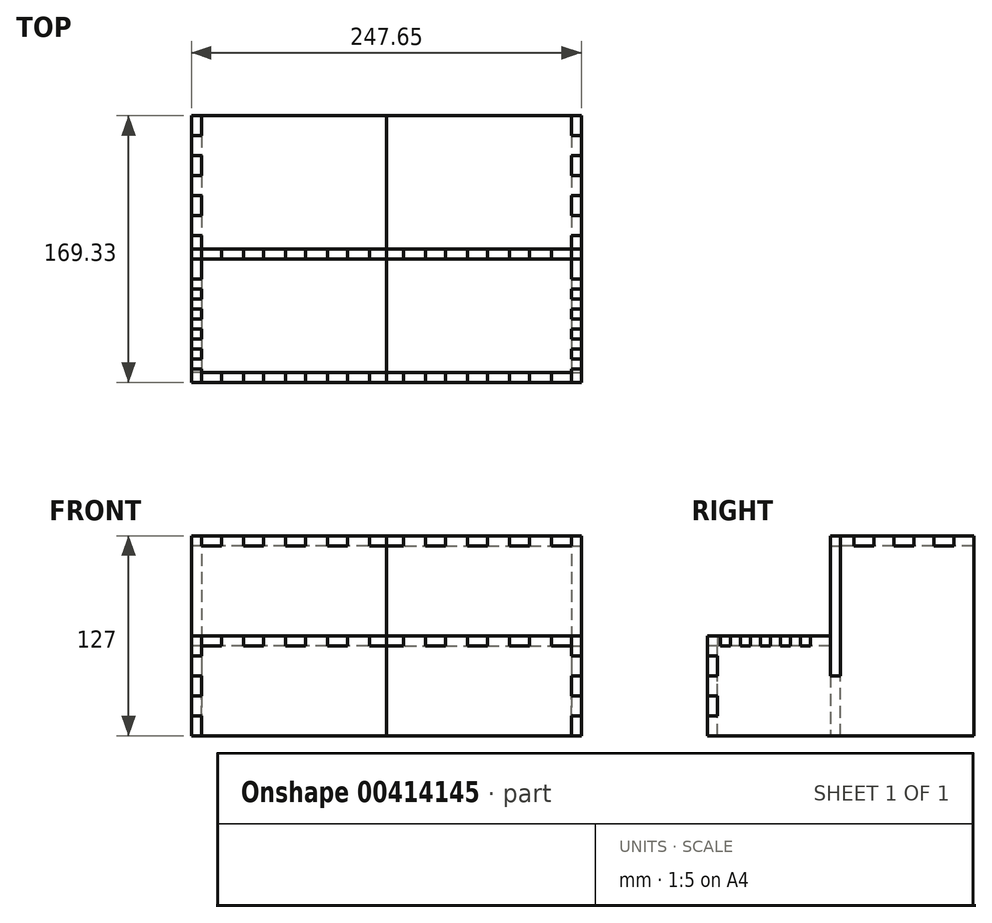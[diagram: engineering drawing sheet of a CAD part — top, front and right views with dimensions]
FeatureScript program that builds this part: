
annotation { "Feature Type Name" : "Feature", "Feature Type Description" : "" }
export const myFeature = defineFeature(function(context is Context, id is Id, definition is map)
    precondition{}
    {
        {
            var Q0;
            Q0=qCreatedBy(makeId("Front.planeOp"),FACE);
            cPlane(context, id + "F0", {"entities" : qUnion([Q0]), "cplaneType" : CPlaneType.OFFSET, "offset" : 84.67 * mm, "oppositeDirection" : true, "width" : 152.4 * mm, "height" : 152.4 * mm});
        }
        {
            var Q0;
            Q0=qCreatedBy(id+"F0.planeOp",FACE);
            cPlane(context, id + "F1", {"entities" : qUnion([Q0]), "cplaneType" : CPlaneType.OFFSET, "offset" : 84.67 * mm, "oppositeDirection" : true, "width" : 152.4 * mm, "height" : 152.4 * mm});
        }
        {
            var Q0;
            Q0=qCreatedBy(makeId("Top.planeOp"),FACE);
            cPlane(context, id + "F2", {"entities" : qUnion([Q0]), "cplaneType" : CPlaneType.OFFSET, "offset" : 127 * mm, "oppositeDirection" : true, "width" : 152.4 * mm, "height" : 152.4 * mm});
        }
        {
            var Q0;
            Q0=qCreatedBy(id+"F2.planeOp",FACE);
            cPlane(context, id + "F3", {"entities" : qUnion([Q0]), "cplaneType" : CPlaneType.OFFSET, "offset" : 63.5 * mm, "width" : 152.4 * mm, "height" : 152.4 * mm});
        }
        {
            var Q0;
            Q0=qCreatedBy(makeId("Right.planeOp"),FACE);
            cPlane(context, id + "F4", {"entities" : qUnion([Q0]), "cplaneType" : CPlaneType.OFFSET, "offset" : 247.65 * mm, "oppositeDirection" : true, "width" : 152.4 * mm, "height" : 152.4 * mm});
        }
        {
            var Q0;
            Q0=qCreatedBy(id+"F4.planeOp",FACE);
            cPlane(context, id + "F5", {"entities" : qUnion([Q0]), "cplaneType" : CPlaneType.OFFSET, "offset" : 123.82 * mm, "width" : 152.4 * mm, "height" : 152.4 * mm});
        }
        {
            var Q0;
            Q0=qCreatedBy(id+"F2.planeOp",FACE);
            var sketch = newSketch(context, id + "F6", { "sketchPlane" : qUnion([Q0])});
            skLineSegment(sketch, "E0", {"start": v(-247.65, 169.33) * mm, "end": v(-247.65, 0) * mm});
            skLineSegment(sketch, "E1", {"start": v(-241.3, 169.33) * mm, "end": v(-241.3, 0) * mm});
            skLineSegment(sketch, "E2", {"start": v(-247.65, 169.33) * mm, "end": v(-241.3, 169.33) * mm});
            skLineSegment(sketch, "E3", {"start": v(-247.65, 0) * mm, "end": v(-241.3, 0) * mm});
            skSolve(sketch);
        }
        {
            var Q0;
            Q0=makeQuery(id+"F6.imprint","IMPRINT",FACE,{"disambiguationData":[TD([[makeQuery(id+"F6.imprint","IMPRINT",EDGE,{"derivedFrom":sQuery(id+"F6.wireOp",EDGE,"E0")}),1.0]])]});
            var Q1;
            Q1=sQuery(id+"F6.wireOp",EDGE,"E0");
            var Q2;
            Q2=qCreatedBy(makeId("Top.planeOp"),FACE);
            extrude(context, id + "F7", {"entities" : qUnion([Q0]), "surfaceEntities" : qUnion([Q1]), "endBound" : BoundingType.UP_TO_SURFACE, "endBoundEntityFace" : qUnion([Q2]), "depth" : 25.4 * mm});
        }
        {
            var Q0;
            Q0=qCreatedBy(id+"F4.planeOp",FACE);
            var sketch = newSketch(context, id + "F8", { "sketchPlane" : qUnion([Q0])});
            skLineSegment(sketch, "E4", {"start": v(0, -63.5) * mm, "end": v(84.67, -63.5) * mm});
            skLineSegment(sketch, "E5", {"start": v(84.67, -63.5) * mm, "end": v(84.67, 0) * mm});
            skLineSegment(sketch, "E6", {"start": v(84.67, 0) * mm, "end": v(0, 0) * mm});
            skLineSegment(sketch, "E7", {"start": v(0, 0) * mm, "end": v(0, -63.5) * mm});
            skLineSegment(sketch, "E8", {"start": v(84.67, -63.5) * mm, "end": v(84.67, -88.9) * mm});
            skLineSegment(sketch, "E9", {"start": v(84.67, -88.9) * mm, "end": v(78.32, -88.9) * mm});
            skLineSegment(sketch, "E10", {"start": v(78.32, -88.9) * mm, "end": v(78.32, -63.5) * mm});
            skLineSegment(sketch, "E11", {"start": v(156.63, 0) * mm, "end": v(156.63, -6.35) * mm});
            skLineSegment(sketch, "E12", {"start": v(156.63, -6.35) * mm, "end": v(143.93, -6.35) * mm});
            skLineSegment(sketch, "E13", {"start": v(143.93, -6.35) * mm, "end": v(143.93, 0) * mm});
            skLineSegment(sketch, "E14", {"start": v(156.63, 0) * mm, "end": v(143.93, 0) * mm});
            skLineSegment(sketch, "E15.1.0.0", {"start": v(131.23, 0) * mm, "end": v(118.53, 0) * mm});
            skLineSegment(sketch, "E15.1.0.1", {"start": v(118.53, -6.35) * mm, "end": v(118.53, 0) * mm});
            skLineSegment(sketch, "E15.1.0.2", {"start": v(131.23, 0) * mm, "end": v(131.23, -6.35) * mm});
            skLineSegment(sketch, "E15.1.0.3", {"start": v(131.23, -6.35) * mm, "end": v(118.53, -6.35) * mm});
            skLineSegment(sketch, "E15.2.0.0", {"start": v(105.83, 0) * mm, "end": v(93.13, 0) * mm});
            skLineSegment(sketch, "E15.2.0.1", {"start": v(93.13, -6.35) * mm, "end": v(93.13, 0) * mm});
            skLineSegment(sketch, "E15.2.0.2", {"start": v(105.83, 0) * mm, "end": v(105.83, -6.35) * mm});
            skLineSegment(sketch, "E15.2.0.3", {"start": v(105.83, -6.35) * mm, "end": v(93.13, -6.35) * mm});
            skLineSegment(sketch, "E15.direction1", {"start": v(143.93, -6.35) * mm, "end": v(118.53, -6.35) * mm, "construction": true});
            skLineSegment(sketch, "E15.direction2", {"start": v(143.93, -6.35) * mm, "end": v(143.93, -6.35) * mm});
            skLineSegment(sketch, "E16", {"start": v(0, -76.2) * mm, "end": v(6.35, -76.2) * mm});
            skLineSegment(sketch, "E17", {"start": v(6.35, -76.2) * mm, "end": v(6.35, -88.9) * mm});
            skLineSegment(sketch, "E18", {"start": v(6.35, -88.9) * mm, "end": v(0, -88.9) * mm});
            skLineSegment(sketch, "E19", {"start": v(0, -76.2) * mm, "end": v(0, -88.9) * mm});
            skLineSegment(sketch, "E20.0.1.0", {"start": v(6.35, -101.6) * mm, "end": v(6.35, -114.3) * mm});
            skLineSegment(sketch, "E20.0.1.1", {"start": v(6.35, -114.3) * mm, "end": v(0, -114.3) * mm});
            skLineSegment(sketch, "E20.0.1.2", {"start": v(0, -101.6) * mm, "end": v(6.35, -101.6) * mm});
            skLineSegment(sketch, "E20.0.1.3", {"start": v(0, -101.6) * mm, "end": v(0, -114.3) * mm});
            skLineSegment(sketch, "E20.direction1", {"start": v(0, -88.9) * mm, "end": v(25.4, -88.9) * mm, "construction": true});
            skLineSegment(sketch, "E20.direction2", {"start": v(0, -88.9) * mm, "end": v(0, -114.3) * mm, "construction": true});
            skLineSegment(sketch, "E21.bottom", {"start": v(65.62, -63.5) * mm, "end": v(59.27, -63.5) * mm});
            skLineSegment(sketch, "E21.top", {"start": v(65.62, -69.85) * mm, "end": v(59.27, -69.85) * mm});
            skLineSegment(sketch, "E21.left", {"start": v(65.62, -63.5) * mm, "end": v(65.62, -69.85) * mm});
            skLineSegment(sketch, "E21.right", {"start": v(59.27, -63.5) * mm, "end": v(59.27, -69.85) * mm});
            skLineSegment(sketch, "E22.1.0.0", {"start": v(52.92, -63.5) * mm, "end": v(52.92, -69.85) * mm});
            skLineSegment(sketch, "E22.1.0.1", {"start": v(52.92, -69.85) * mm, "end": v(46.57, -69.85) * mm});
            skLineSegment(sketch, "E22.1.0.2", {"start": v(46.57, -63.5) * mm, "end": v(46.57, -69.85) * mm});
            skLineSegment(sketch, "E22.2.0.0", {"start": v(40.22, -63.5) * mm, "end": v(40.22, -69.85) * mm});
            skLineSegment(sketch, "E22.2.0.1", {"start": v(40.22, -69.85) * mm, "end": v(33.87, -69.85) * mm});
            skLineSegment(sketch, "E22.2.0.2", {"start": v(33.87, -63.5) * mm, "end": v(33.87, -69.85) * mm});
            skLineSegment(sketch, "E22.3.0.0", {"start": v(27.52, -63.5) * mm, "end": v(27.52, -69.85) * mm});
            skLineSegment(sketch, "E22.3.0.1", {"start": v(27.52, -69.85) * mm, "end": v(21.17, -69.85) * mm});
            skLineSegment(sketch, "E22.3.0.2", {"start": v(21.17, -63.5) * mm, "end": v(21.17, -69.85) * mm});
            skLineSegment(sketch, "E22.4.0.0", {"start": v(14.82, -63.5) * mm, "end": v(14.82, -69.85) * mm});
            skLineSegment(sketch, "E22.4.0.1", {"start": v(14.82, -69.85) * mm, "end": v(8.47, -69.85) * mm});
            skLineSegment(sketch, "E22.4.0.2", {"start": v(8.47, -63.5) * mm, "end": v(8.47, -69.85) * mm});
            skLineSegment(sketch, "E22.direction1", {"start": v(59.27, -69.85) * mm, "end": v(46.57, -69.85) * mm, "construction": true});
            skSolve(sketch);
        }
        {
            var Q0;
            Q0 = qSketchRegion(id + "F8", true);
            var Q1;
            Q1=makeQuery(id+"F7.opExtrude","SWEPT_FACE",FACE,{"disambiguationData":[OSD([sQuery(id+"F6.wireOp",EDGE,"E1")])]});
            extrude(context, id + "F9", {"entities" : qUnion([Q0]), "operationType" : NewBodyOperationType.REMOVE, "endBound" : BoundingType.UP_TO_SURFACE, "endBoundEntityFace" : qUnion([Q1]), "depth" : 25.4 * mm});
        }
        {
            var Q0;
            Q0=qCreatedBy(id+"F4.planeOp",FACE);
            var sketch = newSketch(context, id + "F10", { "sketchPlane" : qUnion([Q0])});
            skLineSegment(sketch, "E23", {"start": v(84.67, 0) * mm, "end": v(78.32, 0) * mm});
            skLineSegment(sketch, "E24", {"start": v(78.32, 0) * mm, "end": v(78.32, -127) * mm});
            skLineSegment(sketch, "E25", {"start": v(78.32, -127) * mm, "end": v(84.67, -127) * mm});
            skLineSegment(sketch, "E26", {"start": v(84.67, -127) * mm, "end": v(84.67, 0) * mm});
            skSolve(sketch);
        }
        {
            var Q0;
            Q0 = qSketchRegion(id + "F10", true);
            var Q1;
            Q1=qCreatedBy(id+"F5.planeOp",FACE);
            extrude(context, id + "F11", {"entities" : qUnion([Q0]), "endBound" : BoundingType.UP_TO_SURFACE, "endBoundEntityFace" : qUnion([Q1]), "depth" : 25.4 * mm});
        }
        {
            var Q0;
            Q0=makeQuery(id+"F7.opExtrude","SWEPT_BODY",BODY,{"disambiguationData":[OSD([sQuery(id+"F6.wireOp",EDGE,"E0"),sQuery(id+"F6.wireOp",EDGE,"E1"),sQuery(id+"F6.wireOp",EDGE,"E2"),sQuery(id+"F6.wireOp",EDGE,"E3")])]});
            var Q1;
            Q1=makeQuery(id+"F11.opExtrude","SWEPT_BODY",BODY,{"disambiguationData":[OSD([sQuery(id+"F10.wireOp",EDGE,"E23"),sQuery(id+"F10.wireOp",EDGE,"E24"),sQuery(id+"F10.wireOp",EDGE,"E25"),sQuery(id+"F10.wireOp",EDGE,"E26")])]});
            booleanBodies(context, id + "F12", {"operationType" : BooleanOperationType.SUBTRACTION, "tools" : qUnion([Q0]), "targets" : qUnion([Q1]), "keepTools" : true});
        }
        {
            var Q0;
            Q0=qCreatedBy(id+"F4.planeOp",FACE);
            var sketch = newSketch(context, id + "F13", { "sketchPlane" : qUnion([Q0])});
            skLineSegment(sketch, "E27.bottom", {"start": v(169.33, 0) * mm, "end": v(78.32, 0) * mm});
            skLineSegment(sketch, "E27.top", {"start": v(169.33, -6.35) * mm, "end": v(78.32, -6.35) * mm});
            skLineSegment(sketch, "E27.left", {"start": v(169.33, 0) * mm, "end": v(169.33, -6.35) * mm});
            skLineSegment(sketch, "E27.right", {"start": v(78.32, 0) * mm, "end": v(78.32, -6.35) * mm});
            skLineSegment(sketch, "E28.bottom", {"start": v(78.32, -63.5) * mm, "end": v(6.35, -63.5) * mm});
            skLineSegment(sketch, "E28.right", {"start": v(6.35, -63.5) * mm, "end": v(6.35, -69.85) * mm});
            skLineSegment(sketch, "E29.bottom", {"start": v(0, -127) * mm, "end": v(6.35, -127) * mm});
            skLineSegment(sketch, "E29.top", {"start": v(0, -63.5) * mm, "end": v(6.35, -63.5) * mm});
            skLineSegment(sketch, "E29.left", {"start": v(0, -127) * mm, "end": v(0, -63.5) * mm});
            skLineSegment(sketch, "E29.right", {"start": v(6.35, -127) * mm, "end": v(6.35, -63.5) * mm});
            skLineSegment(sketch, "E30", {"start": v(78.32, -63.5) * mm, "end": v(78.32, -69.85) * mm});
            skLineSegment(sketch, "E31", {"start": v(78.32, -69.85) * mm, "end": v(0, -69.85) * mm});
            skSolve(sketch);
        }
        {
            var Q0;
            Q0=makeQuery(id+"F13.imprint","IMPRINT",FACE,{"disambiguationData":[TD([[makeQuery(id+"F13.imprint","IMPRINT",EDGE,{"derivedFrom":sQuery(id+"F13.wireOp",EDGE,"E27.bottom")}),1.0]])]});
            var Q1;
            {var subQ0=sQuery(id+"F13.wireOp",EDGE,"E28.bottom");Q1=makeQuery(id+"F13.imprint","IMPRINT",FACE,{"disambiguationData":[TD([[makeQuery(id+"F13.imprint","IMPRINT",EDGE,{"derivedFrom":subQ0}),1.0]])]});}
            var Q2;
            {var subQ0=sQuery(id+"F13.wireOp",EDGE,"E29.top");Q2=makeQuery(id+"F13.imprint","IMPRINT",FACE,{"disambiguationData":[TD([[makeQuery(id+"F13.imprint","IMPRINT",EDGE,{"derivedFrom":subQ0}),-1.0]])]});}
            var Q3;
            Q3=qCreatedBy(id+"F5.planeOp",FACE);
            extrude(context, id + "F14", {"entities" : qUnion([Q0, Q1, Q2]), "endBound" : BoundingType.UP_TO_SURFACE, "endBoundEntityFace" : qUnion([Q3]), "depth" : 25.4 * mm});
        }
        {
            var Q0;
            {var subQ2=sQuery(id+"F13.wireOp",EDGE,"E29.bottom");Q0=makeQuery(id+"F13.imprint","IMPRINT",FACE,{"disambiguationData":[TD([[makeQuery(id+"F13.imprint","IMPRINT",EDGE,{"derivedFrom":subQ2}),1.0]])]});}
            var Q1;
            {var subQ0=sQuery(id+"F13.wireOp",EDGE,"E29.top");Q1=makeQuery(id+"F13.imprint","IMPRINT",FACE,{"disambiguationData":[TD([[makeQuery(id+"F13.imprint","IMPRINT",EDGE,{"derivedFrom":subQ0}),-1.0]])]});}
            var Q2;
            Q2=qCreatedBy(id+"F5.planeOp",FACE);
            extrude(context, id + "F15", {"entities" : qUnion([Q0, Q1]), "endBound" : BoundingType.UP_TO_SURFACE, "endBoundEntityFace" : qUnion([Q2]), "depth" : 25.4 * mm});
        }
        {
            var Q0;
            Q0=makeQuery(id+"F7.opExtrude","SWEPT_BODY",BODY,{"disambiguationData":[OSD([sQuery(id+"F6.wireOp",EDGE,"E0"),sQuery(id+"F6.wireOp",EDGE,"E1"),sQuery(id+"F6.wireOp",EDGE,"E2"),sQuery(id+"F6.wireOp",EDGE,"E3")])]});
            var Q1;
            Q1=makeQuery(id+"F14.opExtrude","SWEPT_BODY",BODY,{"disambiguationData":[OSD([sQuery(id+"F13.wireOp",EDGE,"E27.bottom"),sQuery(id+"F13.wireOp",EDGE,"E27.top"),sQuery(id+"F13.wireOp",EDGE,"E27.left"),sQuery(id+"F13.wireOp",EDGE,"E27.right")])]});
            var Q2;
            Q2=makeQuery(id+"F14.opExtrude","SWEPT_BODY",BODY,{"disambiguationData":[OSD([sQuery(id+"F13.wireOp",EDGE,"E28.bottom"),sQuery(id+"F13.wireOp",EDGE,"E28.top"),sQuery(id+"F13.wireOp",EDGE,"E28.left"),sQuery(id+"F13.wireOp",EDGE,"E29.right")])]});
            var Q3;
            Q3=makeQuery(id+"F15.opExtrude","SWEPT_BODY",BODY,{"disambiguationData":[OSD([sQuery(id+"F13.wireOp",EDGE,"E29.bottom"),sQuery(id+"F13.wireOp",EDGE,"E29.left"),sQuery(id+"F13.wireOp",EDGE,"E29.right"),sQuery(id+"F13.wireOp",EDGE,"E31")])]});
            booleanBodies(context, id + "F16", {"operationType" : BooleanOperationType.SUBTRACTION, "tools" : qUnion([Q0]), "targets" : qUnion([Q1, Q2, Q3]), "keepTools" : true});
        }
        {
            var Q0;
            Q0=qCreatedBy(makeId("Front.planeOp"),FACE);
            var sketch = newSketch(context, id + "F17", { "sketchPlane" : qUnion([Q0])});
            skLineSegment(sketch, "E32.bottom", {"start": v(-241.3, -69.85) * mm, "end": v(-228.6, -69.85) * mm});
            skLineSegment(sketch, "E32.top", {"start": v(-241.3, -63.5) * mm, "end": v(-228.6, -63.5) * mm});
            skLineSegment(sketch, "E32.left", {"start": v(-241.3, -69.85) * mm, "end": v(-241.3, -63.5) * mm});
            skLineSegment(sketch, "E32.right", {"start": v(-228.6, -69.85) * mm, "end": v(-228.6, -63.5) * mm});
            skLineSegment(sketch, "E33.0.1.0", {"start": v(-228.6, -6.35) * mm, "end": v(-228.6, 0) * mm});
            skLineSegment(sketch, "E33.0.1.1", {"start": v(-241.3, 0) * mm, "end": v(-228.6, 0) * mm});
            skLineSegment(sketch, "E33.0.1.2", {"start": v(-241.3, -6.35) * mm, "end": v(-228.6, -6.35) * mm});
            skLineSegment(sketch, "E33.0.1.3", {"start": v(-241.3, -6.35) * mm, "end": v(-241.3, 0) * mm});
            skLineSegment(sketch, "E33.1.0.0", {"start": v(-201.93, -69.85) * mm, "end": v(-201.93, -63.5) * mm});
            skLineSegment(sketch, "E33.1.0.1", {"start": v(-214.63, -63.5) * mm, "end": v(-201.93, -63.5) * mm});
            skLineSegment(sketch, "E33.1.0.2", {"start": v(-214.63, -69.85) * mm, "end": v(-201.93, -69.85) * mm});
            skLineSegment(sketch, "E33.1.0.3", {"start": v(-214.63, -69.85) * mm, "end": v(-214.63, -63.5) * mm});
            skLineSegment(sketch, "E33.1.1.0", {"start": v(-201.93, -6.35) * mm, "end": v(-201.93, 0) * mm});
            skLineSegment(sketch, "E33.1.1.1", {"start": v(-214.63, 0) * mm, "end": v(-201.93, 0) * mm});
            skLineSegment(sketch, "E33.1.1.2", {"start": v(-214.63, -6.35) * mm, "end": v(-201.93, -6.35) * mm});
            skLineSegment(sketch, "E33.1.1.3", {"start": v(-214.63, -6.35) * mm, "end": v(-214.63, 0) * mm});
            skLineSegment(sketch, "E33.2.0.0", {"start": v(-175.26, -69.85) * mm, "end": v(-175.26, -63.5) * mm});
            skLineSegment(sketch, "E33.2.0.1", {"start": v(-187.96, -63.5) * mm, "end": v(-175.26, -63.5) * mm});
            skLineSegment(sketch, "E33.2.0.2", {"start": v(-187.96, -69.85) * mm, "end": v(-175.26, -69.85) * mm});
            skLineSegment(sketch, "E33.2.0.3", {"start": v(-187.96, -69.85) * mm, "end": v(-187.96, -63.5) * mm});
            skLineSegment(sketch, "E33.2.1.0", {"start": v(-175.26, -6.35) * mm, "end": v(-175.26, 0) * mm});
            skLineSegment(sketch, "E33.2.1.1", {"start": v(-187.96, 0) * mm, "end": v(-175.26, 0) * mm});
            skLineSegment(sketch, "E33.2.1.2", {"start": v(-187.96, -6.35) * mm, "end": v(-175.26, -6.35) * mm});
            skLineSegment(sketch, "E33.2.1.3", {"start": v(-187.96, -6.35) * mm, "end": v(-187.96, 0) * mm});
            skLineSegment(sketch, "E33.3.0.0", {"start": v(-148.6, -69.85) * mm, "end": v(-148.6, -63.5) * mm});
            skLineSegment(sketch, "E33.3.0.1", {"start": v(-161.3, -63.5) * mm, "end": v(-148.59, -63.5) * mm});
            skLineSegment(sketch, "E33.3.0.2", {"start": v(-161.3, -69.85) * mm, "end": v(-148.59, -69.85) * mm});
            skLineSegment(sketch, "E33.3.0.3", {"start": v(-161.3, -69.85) * mm, "end": v(-161.3, -63.5) * mm});
            skLineSegment(sketch, "E33.3.1.0", {"start": v(-148.6, -6.35) * mm, "end": v(-148.6, 0) * mm});
            skLineSegment(sketch, "E33.3.1.1", {"start": v(-161.3, 0) * mm, "end": v(-148.59, 0) * mm});
            skLineSegment(sketch, "E33.3.1.2", {"start": v(-161.3, -6.35) * mm, "end": v(-148.59, -6.35) * mm});
            skLineSegment(sketch, "E33.3.1.3", {"start": v(-161.3, -6.35) * mm, "end": v(-161.3, 0) * mm});
            skLineSegment(sketch, "E33.4.0.0", {"start": v(-121.92, -69.85) * mm, "end": v(-121.92, -63.5) * mm});
            skLineSegment(sketch, "E33.4.0.1", {"start": v(-134.62, -63.5) * mm, "end": v(-121.92, -63.5) * mm});
            skLineSegment(sketch, "E33.4.0.2", {"start": v(-134.62, -69.85) * mm, "end": v(-121.92, -69.85) * mm});
            skLineSegment(sketch, "E33.4.0.3", {"start": v(-134.62, -69.85) * mm, "end": v(-134.62, -63.5) * mm});
            skLineSegment(sketch, "E33.4.1.0", {"start": v(-121.92, -6.35) * mm, "end": v(-121.92, 0) * mm});
            skLineSegment(sketch, "E33.4.1.1", {"start": v(-134.62, 0) * mm, "end": v(-121.92, 0) * mm});
            skLineSegment(sketch, "E33.4.1.2", {"start": v(-134.62, -6.35) * mm, "end": v(-121.92, -6.35) * mm});
            skLineSegment(sketch, "E33.4.1.3", {"start": v(-134.62, -6.35) * mm, "end": v(-134.62, 0) * mm});
            skLineSegment(sketch, "E33.direction1", {"start": v(-241.3, -69.85) * mm, "end": v(-214.63, -69.85) * mm, "construction": true});
            skLineSegment(sketch, "E33.direction2", {"start": v(-241.3, -69.85) * mm, "end": v(-241.3, -6.35) * mm, "construction": true});
            skSolve(sketch);
        }
        {
            var Q0;
            Q0=makeQuery(id+"F17.imprint","IMPRINT",FACE,{"disambiguationData":[TD([[makeQuery(id+"F17.imprint","IMPRINT",EDGE,{"derivedFrom":sQuery(id+"F17.wireOp",EDGE,"E32.bottom")}),1.0]])]});
            var Q1;
            Q1=makeQuery(id+"F17.imprint","IMPRINT",FACE,{"disambiguationData":[TD([[makeQuery(id+"F17.imprint","IMPRINT",EDGE,{"derivedFrom":sQuery(id+"F17.wireOp",EDGE,"E33.1.0.0")}),1.0]])]});
            var Q2;
            Q2=makeQuery(id+"F17.imprint","IMPRINT",FACE,{"disambiguationData":[TD([[makeQuery(id+"F17.imprint","IMPRINT",EDGE,{"derivedFrom":sQuery(id+"F17.wireOp",EDGE,"E33.2.0.0")}),1.0]])]});
            var Q3;
            Q3=makeQuery(id+"F17.imprint","IMPRINT",FACE,{"disambiguationData":[TD([[makeQuery(id+"F17.imprint","IMPRINT",EDGE,{"derivedFrom":sQuery(id+"F17.wireOp",EDGE,"E33.3.0.0")}),1.0]])]});
            var Q4;
            Q4=makeQuery(id+"F17.imprint","IMPRINT",FACE,{"disambiguationData":[TD([[makeQuery(id+"F17.imprint","IMPRINT",EDGE,{"derivedFrom":sQuery(id+"F17.wireOp",EDGE,"E33.4.0.0")}),1.0]])]});
            var Q5;
            Q5=makeQuery(id+"F15.opExtrude","SWEPT_FACE",FACE,{"disambiguationData":[OSD([sQuery(id+"F13.wireOp",EDGE,"E29.right")])]});
            extrude(context, id + "F18", {"entities" : qUnion([Q0, Q1, Q2, Q3, Q4]), "operationType" : NewBodyOperationType.REMOVE, "endBound" : BoundingType.UP_TO_SURFACE, "oppositeDirection" : true, "endBoundEntityFace" : qUnion([Q5]), "depth" : 25.4 * mm});
        }
        {
            var Q0;
            Q0=makeQuery(id+"F17.imprint","IMPRINT",FACE,{"disambiguationData":[TD([[makeQuery(id+"F17.imprint","IMPRINT",EDGE,{"derivedFrom":sQuery(id+"F17.wireOp",EDGE,"E33.0.1.0")}),1.0]])]});
            var Q1;
            Q1=makeQuery(id+"F17.imprint","IMPRINT",FACE,{"disambiguationData":[TD([[makeQuery(id+"F17.imprint","IMPRINT",EDGE,{"derivedFrom":sQuery(id+"F17.wireOp",EDGE,"E33.1.1.0")}),1.0]])]});
            var Q2;
            Q2=makeQuery(id+"F17.imprint","IMPRINT",FACE,{"disambiguationData":[TD([[makeQuery(id+"F17.imprint","IMPRINT",EDGE,{"derivedFrom":sQuery(id+"F17.wireOp",EDGE,"E33.2.1.0")}),1.0]])]});
            var Q3;
            Q3=makeQuery(id+"F17.imprint","IMPRINT",FACE,{"disambiguationData":[TD([[makeQuery(id+"F17.imprint","IMPRINT",EDGE,{"derivedFrom":sQuery(id+"F17.wireOp",EDGE,"E33.3.1.0")}),1.0]])]});
            var Q4;
            Q4=makeQuery(id+"F17.imprint","IMPRINT",FACE,{"disambiguationData":[TD([[makeQuery(id+"F17.imprint","IMPRINT",EDGE,{"derivedFrom":sQuery(id+"F17.wireOp",EDGE,"E33.4.1.0")}),1.0]])]});
            var Q5;
            Q5=makeQuery(id+"F11.opExtrude","SWEPT_FACE",FACE,{"disambiguationData":[OSD([sQuery(id+"F10.wireOp",EDGE,"E26")])]});
            extrude(context, id + "F19", {"entities" : qUnion([Q0, Q1, Q2, Q3, Q4]), "operationType" : NewBodyOperationType.REMOVE, "endBound" : BoundingType.UP_TO_SURFACE, "oppositeDirection" : true, "endBoundEntityFace" : qUnion([Q5]), "depth" : 25.4 * mm});
        }
        {
            var Q0;
            Q0=makeQuery(id+"F15.opExtrude","SWEPT_BODY",BODY,{"disambiguationData":[OSD([sQuery(id+"F13.wireOp",EDGE,"E29.bottom"),sQuery(id+"F13.wireOp",EDGE,"E29.top"),sQuery(id+"F13.wireOp",EDGE,"E29.left"),sQuery(id+"F13.wireOp",EDGE,"E29.right")])]});
            var Q1;
            Q1=makeQuery(id+"F11.opExtrude","SWEPT_BODY",BODY,{"disambiguationData":[OSD([sQuery(id+"F10.wireOp",EDGE,"E23"),sQuery(id+"F10.wireOp",EDGE,"E24"),sQuery(id+"F10.wireOp",EDGE,"E25"),sQuery(id+"F10.wireOp",EDGE,"E26")])]});
            var Q2;
            Q2=makeQuery(id+"F14.opExtrude","SWEPT_BODY",BODY,{"disambiguationData":[OSD([sQuery(id+"F13.wireOp",EDGE,"E28.bottom"),sQuery(id+"F13.wireOp",EDGE,"E29.top"),sQuery(id+"F13.wireOp",EDGE,"E29.left"),sQuery(id+"F13.wireOp",EDGE,"E30"),sQuery(id+"F13.wireOp",EDGE,"E31")])]});
            var Q3;
            Q3=makeQuery(id+"F14.opExtrude","SWEPT_BODY",BODY,{"disambiguationData":[OSD([sQuery(id+"F13.wireOp",EDGE,"E27.bottom"),sQuery(id+"F13.wireOp",EDGE,"E27.top"),sQuery(id+"F13.wireOp",EDGE,"E27.left"),sQuery(id+"F13.wireOp",EDGE,"E27.right")])]});
            booleanBodies(context, id + "F20", {"operationType" : BooleanOperationType.SUBTRACTION, "tools" : qUnion([Q0, Q1]), "targets" : qUnion([Q2, Q3]), "keepTools" : true});
        }
        {
            var Q0;
            Q0=makeQuery(id+"F11.opExtrude","SWEPT_BODY",BODY,{"disambiguationData":[OSD([sQuery(id+"F10.wireOp",EDGE,"E23"),sQuery(id+"F10.wireOp",EDGE,"E24"),sQuery(id+"F10.wireOp",EDGE,"E25"),sQuery(id+"F10.wireOp",EDGE,"E26")])]});
            var Q1;
            Q1=makeQuery(id+"F14.opExtrude","SWEPT_BODY",BODY,{"disambiguationData":[OSD([sQuery(id+"F13.wireOp",EDGE,"E27.bottom"),sQuery(id+"F13.wireOp",EDGE,"E27.top"),sQuery(id+"F13.wireOp",EDGE,"E27.left"),sQuery(id+"F13.wireOp",EDGE,"E27.right")])]});
            var Q2;
            Q2=makeQuery(id+"F14.opExtrude","SWEPT_BODY",BODY,{"disambiguationData":[OSD([sQuery(id+"F13.wireOp",EDGE,"E28.bottom"),sQuery(id+"F13.wireOp",EDGE,"E29.top"),sQuery(id+"F13.wireOp",EDGE,"E29.left"),sQuery(id+"F13.wireOp",EDGE,"E30"),sQuery(id+"F13.wireOp",EDGE,"E31")])]});
            var Q3;
            Q3=makeQuery(id+"F15.opExtrude","SWEPT_BODY",BODY,{"disambiguationData":[OSD([sQuery(id+"F13.wireOp",EDGE,"E29.bottom"),sQuery(id+"F13.wireOp",EDGE,"E29.top"),sQuery(id+"F13.wireOp",EDGE,"E29.left"),sQuery(id+"F13.wireOp",EDGE,"E29.right")])]});
            var Q4;
            Q4=makeQuery(id+"F7.opExtrude","SWEPT_BODY",BODY,{"disambiguationData":[OSD([sQuery(id+"F6.wireOp",EDGE,"E0"),sQuery(id+"F6.wireOp",EDGE,"E1"),sQuery(id+"F6.wireOp",EDGE,"E2"),sQuery(id+"F6.wireOp",EDGE,"E3")])]});
            var Q5;
            Q5=qCreatedBy(id+"F5.planeOp",FACE);
            mirror(context, id + "F21", {"entities" : qUnion([Q0, Q1, Q2, Q3, Q4]), "mirrorPlane" : qUnion([Q5])});
        }
    });
